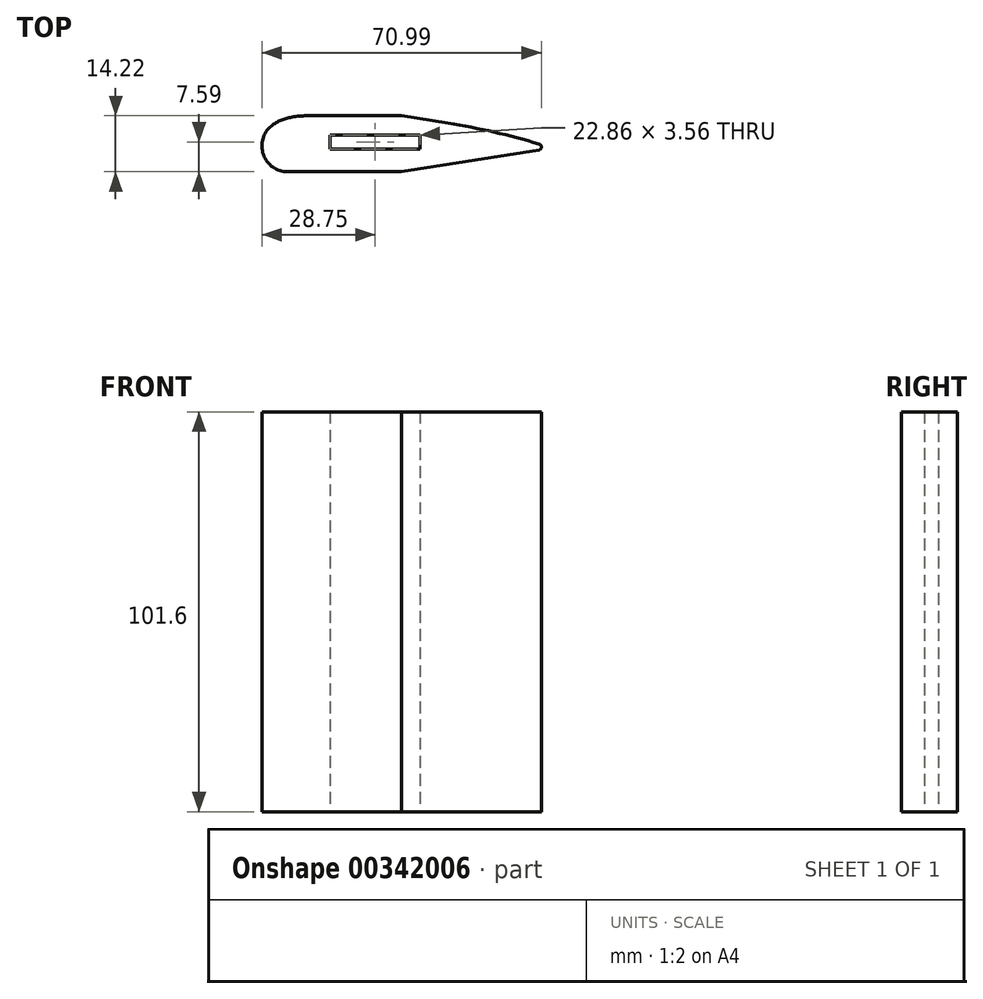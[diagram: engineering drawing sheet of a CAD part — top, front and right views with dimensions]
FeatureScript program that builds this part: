
annotation { "Feature Type Name" : "Feature", "Feature Type Description" : "" }
export const myFeature = defineFeature(function(context is Context, id is Id, definition is map)
    precondition{}
    {
        {
            var Q0;
            Q0=qCreatedBy(makeId("Top.planeOp"),FACE);
            var sketch = newSketch(context, id + "F0", { "sketchPlane" : qUnion([Q0])});
            skLineSegment(sketch, "E0.bottom", {"start": v(-11.43, 1.78) * mm, "end": v(11.43, 1.78) * mm});
            skLineSegment(sketch, "E0.top", {"start": v(-11.43, -1.78) * mm, "end": v(11.43, -1.78) * mm});
            skLineSegment(sketch, "E0.left", {"start": v(-11.43, 1.78) * mm, "end": v(-11.43, -1.78) * mm});
            skLineSegment(sketch, "E0.right", {"start": v(11.43, 1.78) * mm, "end": v(11.43, -1.78) * mm});
            skPoint(sketch, "E0.middle", {"position": v(0, 0) * mm});
            skLineSegment(sketch, "E1.bottom", {"start": v(-30.25, 6.63) * mm, "end": v(44.84, 6.63) * mm});
            skLineSegment(sketch, "E1.top", {"start": v(-30.25, -7.6) * mm, "end": v(44.84, -7.6) * mm});
            skLineSegment(sketch, "E1.left", {"start": v(-30.25, 6.63) * mm, "end": v(-30.25, -7.6) * mm});
            skLineSegment(sketch, "E1.right", {"start": v(44.84, 6.63) * mm, "end": v(44.84, -7.6) * mm});
            skSolve(sketch);
        }
        {
            var Q0;
            Q0=makeQuery(id+"F0.imprint","IMPRINT",FACE,{"disambiguationData":[TD([[makeQuery(id+"F0.imprint","IMPRINT",EDGE,{"derivedFrom":sQuery(id+"F0.wireOp",EDGE,"E0.bottom")}),1.0]])]});
            extrude(context, id + "F1", {"entities" : qUnion([Q0]), "depth" : 101.6 * mm});
        }
        {
            var Q0;
            Q0=makeQuery(id+"F1.opExtrude","SWEPT_EDGE",EDGE,{"disambiguationData":[OSD([sQuery(id+"F0.wireOp",EDGE,"E1.bottom"),sQuery(id+"F0.wireOp",EDGE,"E1.left")])]});
            fillet(context, id + "F2", {"entities" : qUnion([Q0]), "radius" : 12.88 * mm, "tangentPropagation" : true, "rho" : 0.5, "crossSection" : FilletCrossSection.CONIC, "allowEdgeOverflow" : false});
        }
        {
            var Q0;
            Q0=makeQuery(id+"F1.opExtrude","SWEPT_EDGE",EDGE,{"disambiguationData":[OSD([sQuery(id+"F0.wireOp",EDGE,"E1.top"),sQuery(id+"F0.wireOp",EDGE,"E1.left")])]});
            fillet(context, id + "F3", {"entities" : qUnion([Q0]), "radius" : 6.55 * mm, "tangentPropagation" : true, "allowEdgeOverflow" : false});
        }
        {
            var Q0;
            Q0=makeQuery(id+"F1.opExtrude","SWEPT_EDGE",EDGE,{"disambiguationData":[OSD([sQuery(id+"F0.wireOp",EDGE,"E1.bottom"),sQuery(id+"F0.wireOp",EDGE,"E1.right")])]});
            var Q1;
            Q1=makeQuery(id+"F1.opExtrude","SWEPT_EDGE",EDGE,{"disambiguationData":[OSD([sQuery(id+"F0.wireOp",EDGE,"E1.top"),sQuery(id+"F0.wireOp",EDGE,"E1.right")])]});
            chamfer(context, id + "F4", {"entities" : qUnion([Q0, Q1]), "chamferType" : ChamferType.OFFSET_ANGLE, "width" : 38.1 * mm, "oppositeDirection" : false, "angle" : 9 * degree, "tangentPropagation" : true});
        }
        {
            var Q0;
            {var subQ0=sQuery(id+"F0.wireOp",EDGE,"E1.right");Q0=makeQuery(id+"F4.opChamfer","BLEND_EDGE",EDGE,{"blendedFrom":[makeQuery(id+"F1.opExtrude","SWEPT_EDGE",EDGE,{"disambiguationData":[OSD([sQuery(id+"F0.wireOp",EDGE,"E1.bottom"),subQ0])]}),makeQuery(id+"F1.opExtrude","SWEPT_FACE",FACE,{"disambiguationData":[OSD([subQ0])]})],"blendedInto":[makeQuery(id+"F1.opExtrude","SWEPT_FACE",FACE,{"disambiguationData":[OSD([subQ0])]})]});}
            fillet(context, id + "F5", {"entities" : qUnion([Q0]), "radius" : 171.7 * mm, "tangentPropagation" : true, "allowEdgeOverflow" : false});
        }
        {
            var Q0;
            {var subQ0=sQuery(id+"F0.wireOp",EDGE,"E1.right");Q0=makeQuery(id+"F5.opFillet","BLEND_EDGE",EDGE,{"blendedFrom":[makeQuery(id+"F4.opChamfer","BLEND_EDGE",EDGE,{"blendedFrom":[makeQuery(id+"F1.opExtrude","SWEPT_EDGE",EDGE,{"disambiguationData":[OSD([sQuery(id+"F0.wireOp",EDGE,"E1.bottom"),subQ0])]}),makeQuery(id+"F1.opExtrude","SWEPT_FACE",FACE,{"disambiguationData":[OSD([subQ0])]})],"blendedInto":[makeQuery(id+"F1.opExtrude","SWEPT_FACE",FACE,{"disambiguationData":[OSD([subQ0])]})]}),makeQuery(id+"F4.opChamfer","BLEND_FACE",FACE,{"disambiguationData":[OSD([sQuery(id+"F0.wireOp",EDGE,"E1.top"),subQ0])]})],"blendedInto":[makeQuery(id+"F4.opChamfer","BLEND_FACE",FACE,{"disambiguationData":[OSD([sQuery(id+"F0.wireOp",EDGE,"E1.top"),subQ0])]})]});}
            fillet(context, id + "F6", {"entities" : qUnion([Q0]), "radius" : 0.77 * mm, "tangentPropagation" : true, "allowEdgeOverflow" : false});
        }
    });
